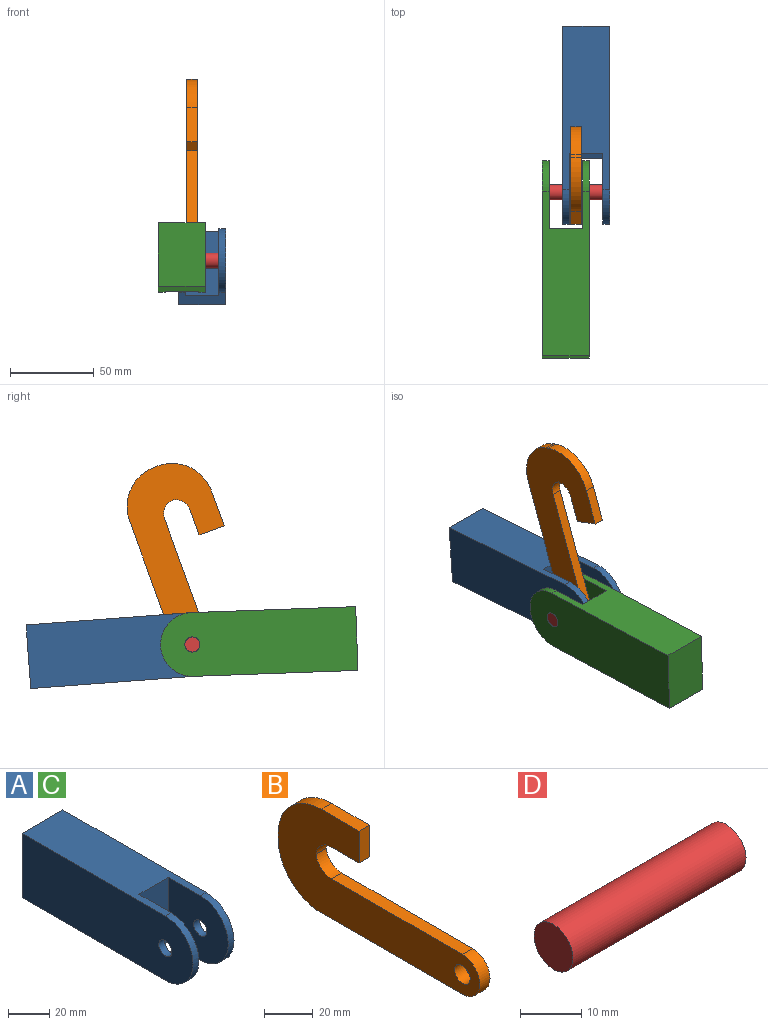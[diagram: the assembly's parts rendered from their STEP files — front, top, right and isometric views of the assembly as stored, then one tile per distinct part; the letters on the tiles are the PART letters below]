
ASSEMBLY  parts=4 mates=3
PART A: 12 faces, bbox 28x117x38 mm
  f0: cylinder r=19mm len=38mm, axis (-1,0,0), area 238.8mm2, adj f2,f4,f5,f9
  f1: plane 117x38mm, normal (-1,0,0), area 4227.4mm2, adj f3,f4,f5,f6,f11
  f2: plane 117x38mm, normal (1,0,0), area 4227.4mm2, adj f0,f3,f4,f5,f10
  f3: plane 38x28mm, normal (0,1,0), area 1064mm2, adj f1,f2,f4,f5
  f4: plane 98x28mm, normal (0,0,1), area 2304mm2, adj f0,f1,f2,f3,f6,f7,f8,f9
  f5: plane 98x28mm, normal (0,0,-1), area 2304mm2, adj f0,f1,f2,f3,f6,f7,f8,f9
  f6: cylinder r=19mm len=38mm, axis (-1,0,0), area 238.8mm2, adj f1,f4,f5,f8
  f7: plane 38x20mm, normal (0,-1,0), area 760mm2, adj f4,f5,f8,f9
  f8: plane 41x38mm, normal (1,0,0), area 1339.4mm2, adj f4,f5,f6,f7,f11
  f9: plane 41x38mm, normal (-1,0,0), area 1339.4mm2, adj f0,f4,f5,f7,f10
  f10: cylinder r=4.5mm len=9mm, axis (1,0,0), area 113.1mm2, adj f2,f9
  f11: cylinder r=4.5mm len=9mm, axis (1,0,0), area 113.1mm2, adj f1,f8
PART B: 14 faces, bbox 6x117x52 mm
  f0: plane 6x2mm, normal (0,1,0), area 12mm2, adj f6,f7,f8,f9
  f1: plane 22x6mm, normal (0,0,1), area 132mm2, adj f2,f6,f7,f9
  f2: plane 16x6mm, normal (0,-1,0), area 96mm2, adj f1,f3,f6,f7
  f3: plane 16x6mm, normal (0,0,-1), area 96mm2, adj f2,f6,f7,f10
  f4: plane 76x6mm, normal (0,0,1), area 456mm2, adj f6,f7,f11,f12
  f5: plane 82x6mm, normal (0,0,-1), area 492mm2, adj f6,f7,f8,f12
  f6: plane 117x52mm, normal (1,0,0), area 3103.9mm2, adj f0,f1,f2,f3,f4,f5,f8,f9
  f7: plane 117x52mm, normal (-1,0,0), area 3103.9mm2, adj f0,f1,f2,f3,f4,f5,f8,f9
  f8: cylinder r=25mm len=25mm, axis (-1,0,0), area 235.6mm2, adj f0,f5,f6,f7
  f9: cylinder r=25mm len=25mm, axis (-1,0,0), area 235.6mm2, adj f0,f1,f6,f7
  f10: cylinder r=9mm len=8.94mm, axis (1,0,0), area 78.8mm2, adj f3,f6,f7,f11
  f11: cylinder r=9mm len=8.94mm, axis (-1,0,0), area 78.8mm2, adj f4,f6,f7,f10
  f12: cylinder r=10mm len=20mm, axis (1,0,0), area 188.5mm2, adj f4,f5,f6,f7
  f13: cylinder r=4.5mm len=9mm, axis (1,0,0), area 169.6mm2, adj f6,f7
PART C: same geometry as A
PART D: 3 faces, bbox 40x9x9 mm
  f0: cylinder r=4.5mm len=40mm, axis (-1,0,0), area 1131mm2, adj f1,f2
  f1: plane 9x9mm, normal (1,0,0), area 63.6mm2, adj f0
  f2: plane 9x9mm, normal (-1,0,0), area 63.6mm2, adj f0
PLACE A rot(axis=(-1,0,0),4.3deg) t=(0.87,-19.69,-24.21)mm
PLACE B rot(axis=(1,0,0),70deg) t=(5.87,6.65,-19.49)mm
PLACE C rot(axis=(1,0,0),177.9deg) t=(-11.13,20.35,11.62)mm
PLACE D t=(-11.13,0.67,-6.67)mm fixed
MATE revolute D.f0 <-> B.f12  axis (-1,0,0) through (8.87,0.67,-6.67)mm
MATE revolute A.f0 <-> D.f0  axis (1,0,0) through (28.87,0.67,-6.67)mm
MATE revolute D.f0 <-> C.f0  axis (-1,0,0) through (-11.13,0.67,-6.67)mm
